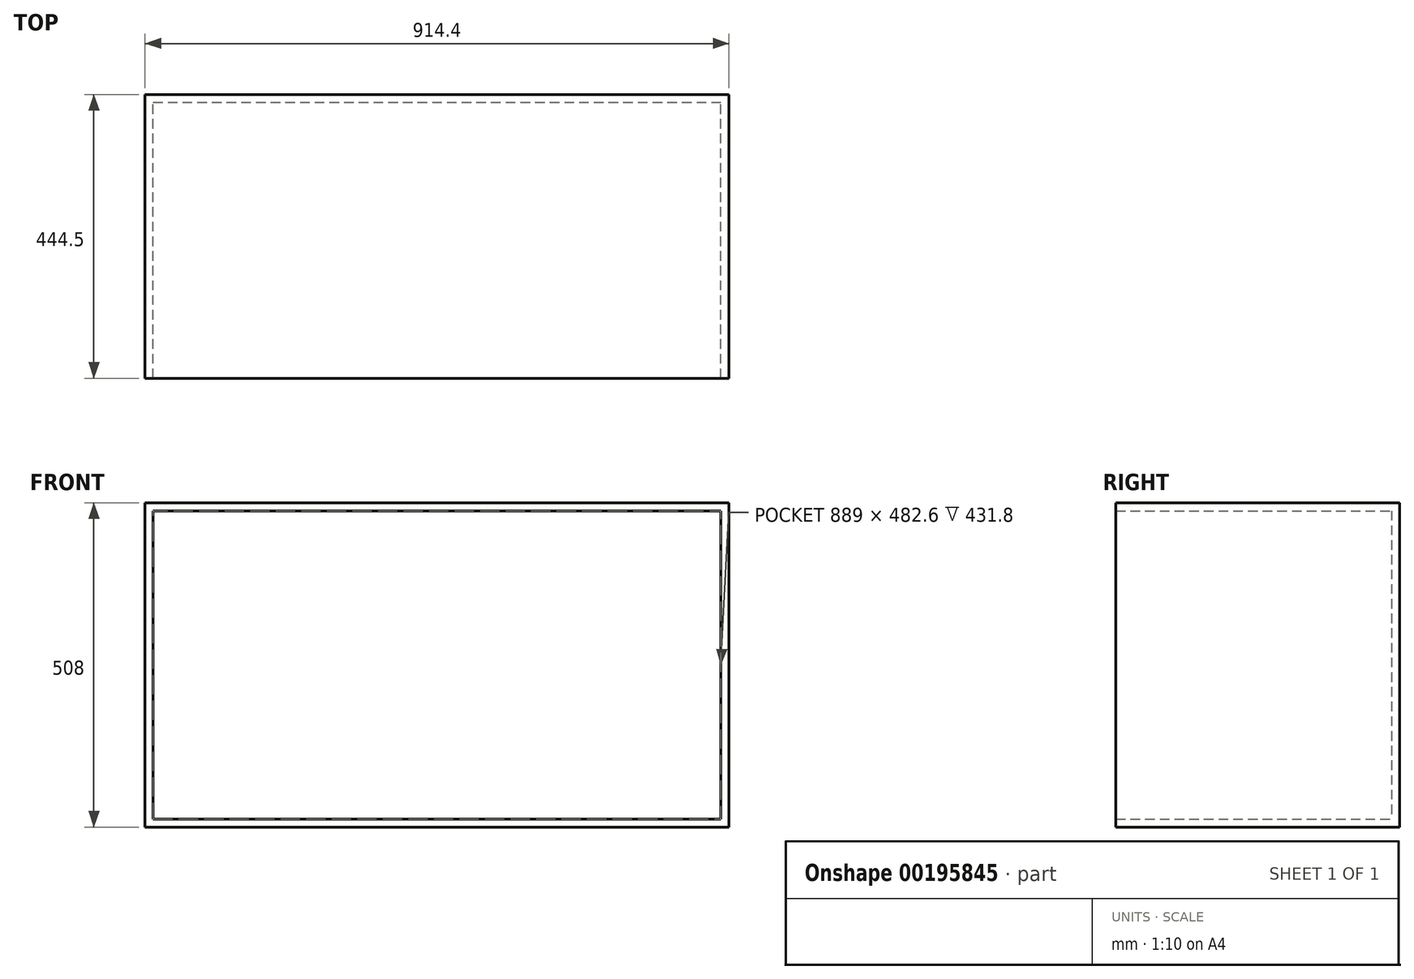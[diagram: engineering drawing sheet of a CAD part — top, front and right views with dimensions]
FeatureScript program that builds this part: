
annotation { "Feature Type Name" : "Feature", "Feature Type Description" : "" }
export const myFeature = defineFeature(function(context is Context, id is Id, definition is map)
    precondition{}
    {
        {
            var Q0;
            Q0=qCreatedBy(makeId("Top.planeOp"),FACE);
            var sketch = newSketch(context, id + "F0", { "sketchPlane" : qUnion([Q0])});
            skLineSegment(sketch, "E0.bottom", {"start": v(457.2, -222.25) * mm, "end": v(-457.2, -222.25) * mm});
            skLineSegment(sketch, "E0.top", {"start": v(457.2, 222.25) * mm, "end": v(-457.2, 222.25) * mm});
            skLineSegment(sketch, "E0.left", {"start": v(457.2, -222.25) * mm, "end": v(457.2, 222.25) * mm});
            skLineSegment(sketch, "E0.right", {"start": v(-457.2, -222.25) * mm, "end": v(-457.2, 222.25) * mm});
            skPoint(sketch, "E0.middle", {"position": v(0, 0) * mm});
            skSolve(sketch);
        }
        {
            var Q0;
            Q0=makeQuery(id+"F0.imprint","IMPRINT",FACE,{"disambiguationData":[TD([[makeQuery(id+"F0.imprint","IMPRINT",EDGE,{"derivedFrom":sQuery(id+"F0.wireOp",EDGE,"E0.bottom")}),-1.0]])]});
            extrude(context, id + "F1", {"entities" : qUnion([Q0]), "depth" : 508 * mm});
        }
        {
            var Q0;
            Q0=makeQuery(id+"F1.opExtrude","SWEPT_FACE",FACE,{"disambiguationData":[OSD([sQuery(id+"F0.wireOp",EDGE,"E0.bottom")])]});
            shell(context, id + "F2", {"entities" : qUnion([Q0]), "thickness" : 12.7 * mm});
        }
    });
